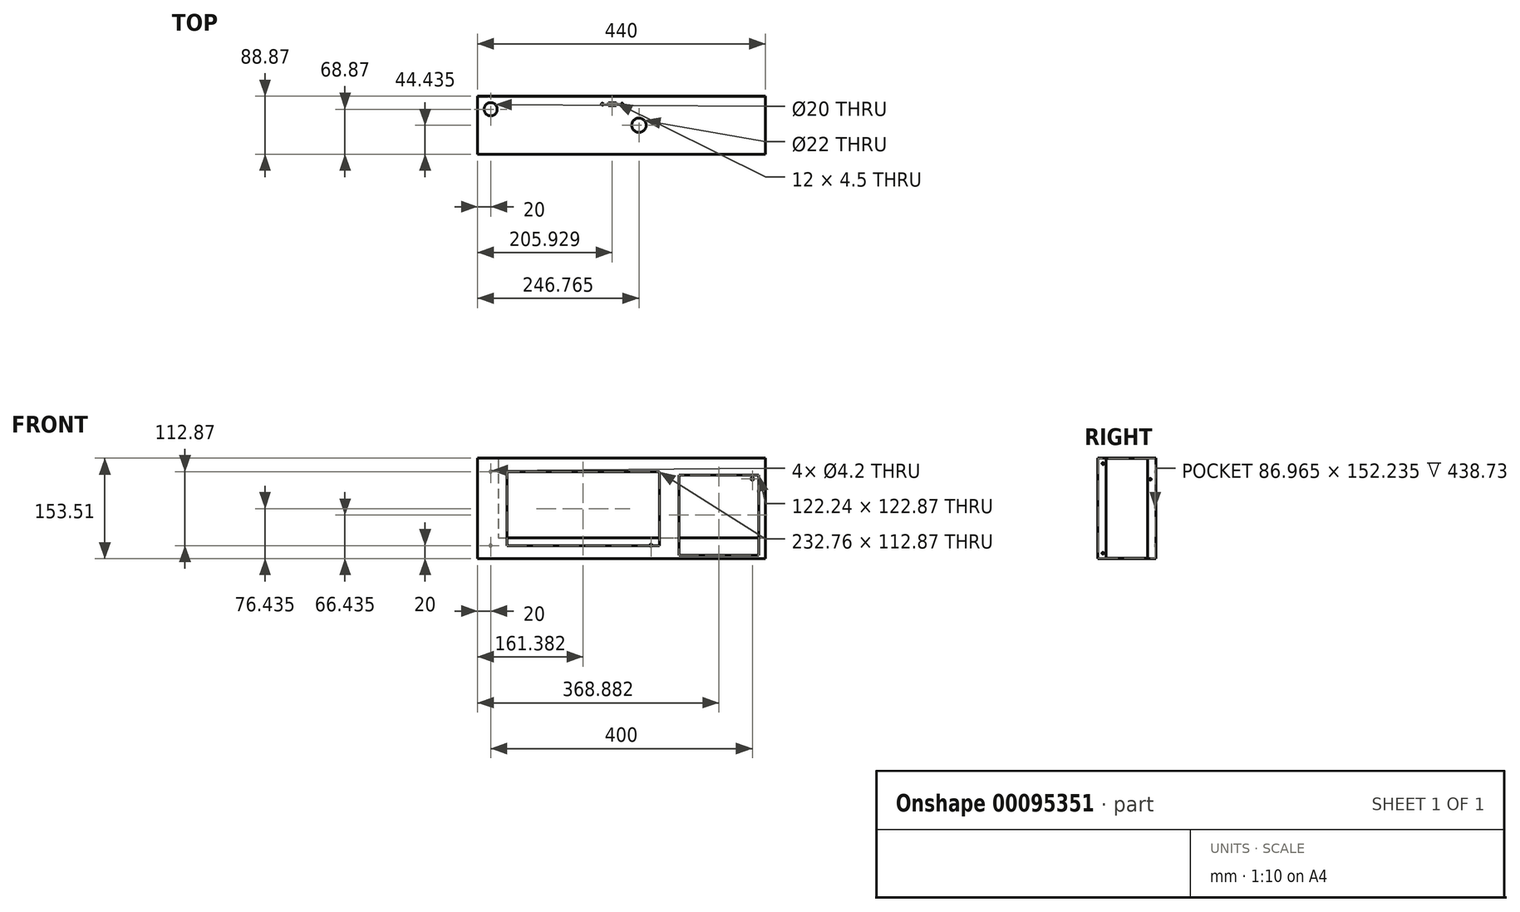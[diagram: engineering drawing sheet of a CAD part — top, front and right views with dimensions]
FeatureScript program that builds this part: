
annotation { "Feature Type Name" : "Feature", "Feature Type Description" : "" }
export const myFeature = defineFeature(function(context is Context, id is Id, definition is map)
    precondition{}
    {
        {
            var Q0;
            Q0=qCreatedBy(makeId("Top.planeOp"),FACE);
            var sketch = newSketch(context, id + "F0", { "sketchPlane" : qUnion([Q0])});
            skLineSegment(sketch, "E0.bottom", {"start": v(0, 0) * mm, "end": v(440, 0) * mm});
            skLineSegment(sketch, "E0.top", {"start": v(0, -88.87) * mm, "end": v(440, -88.87) * mm});
            skLineSegment(sketch, "E0.left", {"start": v(0, 0) * mm, "end": v(0, -88.87) * mm});
            skLineSegment(sketch, "E0.right", {"start": v(440, 0) * mm, "end": v(440, -88.87) * mm});
            skLineSegment(sketch, "E1", {"start": v(297.76, 0) * mm, "end": v(297.76, -88.87) * mm, "construction": true});
            skCircle(sketch, "E2", {"center": v(20, -20) * mm, "radius": 10 * mm});
            skCircle(sketch, "E3", {"center": v(246.76, -44.43) * mm, "radius": 11 * mm});
            skLineSegment(sketch, "E4.bottom", {"start": v(211.93, -14.5) * mm, "end": v(199.93, -14.5) * mm});
            skLineSegment(sketch, "E4.top", {"start": v(211.93, -10) * mm, "end": v(199.93, -10) * mm});
            skLineSegment(sketch, "E4.left", {"start": v(211.93, -14.5) * mm, "end": v(211.93, -10) * mm});
            skLineSegment(sketch, "E4.right", {"start": v(199.93, -14.5) * mm, "end": v(199.93, -10) * mm});
            skPoint(sketch, "E4.middle", {"position": v(205.93, -12.25) * mm});
            skPoint(sketch, "E5", {"position": v(297.76, -44.43) * mm});
            skCircle(sketch, "E6", {"center": v(220.93, -12.25) * mm, "radius": 1.6 * mm});
            skCircle(sketch, "E7", {"center": v(190.93, -12.25) * mm, "radius": 1.6 * mm});
            skLineSegment(sketch, "E8", {"start": v(205.93, -10) * mm, "end": v(205.93, -14.5) * mm, "construction": true});
            skSolve(sketch);
        }
        {
            var Q0;
            Q0=makeQuery(id+"F0.imprint","IMPRINT",FACE,{"disambiguationData":[TD([[makeQuery(id+"F0.imprint","IMPRINT",EDGE,{"derivedFrom":sQuery(id+"F0.wireOp",EDGE,"E0.bottom")}),-1.0]])]});
            extrude(context, id + "F1", {"entities" : qUnion([Q0]), "depth" : .635 * mm});
        }
        {
            var Q0;
            Q0=qCreatedBy(makeId("Front.planeOp"),FACE);
            var sketch = newSketch(context, id + "F2", { "sketchPlane" : qUnion([Q0])});
            skLineSegment(sketch, "E9.0", {"start": v(0, 0) * mm, "end": v(440, 0) * mm});
            skLineSegment(sketch, "E10.top", {"start": v(0, -152.87) * mm, "end": v(440, -152.87) * mm});
            skLineSegment(sketch, "E10.left", {"start": v(0, 0) * mm, "end": v(0, -152.87) * mm});
            skLineSegment(sketch, "E10.right", {"start": v(440, 0) * mm, "end": v(440, -152.87) * mm});
            skCircle(sketch, "E11", {"center": v(20, -20) * mm, "radius": 2.1 * mm});
            skCircle(sketch, "E12", {"center": v(20, -132.87) * mm, "radius": 2.1 * mm});
            skCircle(sketch, "E13", {"center": v(265.14, -132.87) * mm, "radius": 2.1 * mm});
            skPoint(sketch, "E14.0", {"position": v(297.76, 0) * mm});
            skLineSegment(sketch, "E15", {"start": v(297.76, 0) * mm, "end": v(297.76, -152.87) * mm, "construction": true});
            skCircle(sketch, "E16", {"center": v(420, -30.93) * mm, "radius": 2.1 * mm});
            skSolve(sketch);
        }
        {
            var Q0;
            Q0=makeQuery(id+"F2.imprint","IMPRINT",FACE,{"disambiguationData":[TD([[makeQuery(id+"F2.imprint","IMPRINT",EDGE,{"derivedFrom":sQuery(id+"F2.wireOp",EDGE,"E9.0")}),-1.0]])]});
            extrude(context, id + "F3", {"entities" : qUnion([Q0]), "operationType" : NewBodyOperationType.ADD, "depth" : .635 * mm});
        }
        {
            var Q0;
            Q0=makeQuery(id+"F1.opExtrude","SWEPT_FACE",FACE,{"disambiguationData":[OSD([sQuery(id+"F0.wireOp",EDGE,"E0.top")])]});
            var sketch = newSketch(context, id + "F4", { "sketchPlane" : qUnion([Q0])});
            skLineSegment(sketch, "E17.0", {"start": v(0, 0) * mm, "end": v(440, 0) * mm});
            skLineSegment(sketch, "E18.0", {"start": v(0, -152.87) * mm, "end": v(440, -152.87) * mm});
            skLineSegment(sketch, "E19", {"start": v(0, 0.63) * mm, "end": v(0, -152.87) * mm});
            skLineSegment(sketch, "E20", {"start": v(440, 0.63) * mm, "end": v(440, -152.87) * mm});
            skPoint(sketch, "E21.0", {"position": v(297.76, 0) * mm});
            skLineSegment(sketch, "E22", {"start": v(297.76, 0) * mm, "end": v(297.76, -152.87) * mm, "construction": true});
            skLineSegment(sketch, "E23.bottom", {"start": v(45, -20) * mm, "end": v(277.76, -20) * mm});
            skLineSegment(sketch, "E23.top", {"start": v(45, -132.87) * mm, "end": v(277.76, -132.87) * mm});
            skLineSegment(sketch, "E23.left", {"start": v(45, -20) * mm, "end": v(45, -132.87) * mm});
            skLineSegment(sketch, "E23.right", {"start": v(277.76, -20) * mm, "end": v(277.76, -132.87) * mm});
            skLineSegment(sketch, "E24.bottom", {"start": v(307.76, -25) * mm, "end": v(430, -25) * mm});
            skLineSegment(sketch, "E24.top", {"start": v(307.76, -147.87) * mm, "end": v(430, -147.87) * mm});
            skLineSegment(sketch, "E24.left", {"start": v(307.76, -25) * mm, "end": v(307.76, -147.87) * mm});
            skLineSegment(sketch, "E24.right", {"start": v(430, -25) * mm, "end": v(430, -147.87) * mm});
            skSolve(sketch);
        }
        {
            var Q0;
            {var subQ2=sQuery(id+"F4.wireOp",EDGE,"E17.0");Q0=makeQuery(id+"F4.imprint","IMPRINT",FACE,{"disambiguationData":[TD([[makeQuery(id+"F4.imprint","IMPRINT",EDGE,{"derivedFrom":subQ2}),-1.0]])]});}
            extrude(context, id + "F5", {"entities" : qUnion([Q0]), "operationType" : NewBodyOperationType.ADD, "oppositeDirection" : true, "depth" : .635 * mm});
        }
        {
            var Q0;
            Q0=makeQuery(id+"F5.opExtrude","SWEPT_FACE",FACE,{"disambiguationData":[OSD([sQuery(id+"F4.wireOp",EDGE,"E18.0")])]});
            var sketch = newSketch(context, id + "F6", { "sketchPlane" : qUnion([Q0])});
            skLineSegment(sketch, "E25.0", {"start": v(0, 0.64) * mm, "end": v(440, 0.64) * mm});
            skLineSegment(sketch, "E26.0", {"start": v(0, 88.87) * mm, "end": v(440, 88.87) * mm});
            skLineSegment(sketch, "E27", {"start": v(0, 0.63) * mm, "end": v(0, 88.87) * mm});
            skLineSegment(sketch, "E28", {"start": v(440, 88.87) * mm, "end": v(440, 0.63) * mm});
            skSolve(sketch);
        }
        {
            var Q0;
            {var subQ0=sQuery(id+"F6.wireOp",EDGE,"E25.0");Q0=makeQuery(id+"F6.imprint","IMPRINT",FACE,{"disambiguationData":[TD([[makeQuery(id+"F6.imprint","IMPRINT",EDGE,{"derivedFrom":subQ0}),1.0]])]});}
            extrude(context, id + "F7", {"entities" : qUnion([Q0]), "operationType" : NewBodyOperationType.ADD, "oppositeDirection" : true, "depth" : .635 * mm});
        }
        {
            var Q0;
            Q0=makeQuery(id+"F3.opExtrude","CAP_FACE",FACE,{"disambiguationData":[OSD([sQuery(id+"F2.wireOp",EDGE,"E9.0"),sQuery(id+"F2.wireOp",EDGE,"E10.top"),sQuery(id+"F2.wireOp",EDGE,"E10.left"),sQuery(id+"F2.wireOp",EDGE,"E10.right"),sQuery(id+"F2.wireOp",EDGE,"E11"),sQuery(id+"F2.wireOp",EDGE,"E12"),sQuery(id+"F2.wireOp",EDGE,"E13"),sQuery(id+"F2.wireOp",EDGE,"E16")])],"isStart":false});
            var sketch = newSketch(context, id + "F8", { "sketchPlane" : qUnion([Q0])});
            skLineSegment(sketch, "E29.0", {"start": v(0, -152.24) * mm, "end": v(440, -152.24) * mm});
            skCircle(sketch, "E30.0", {"center": v(20, -132.87) * mm, "radius": 2.1 * mm});
            skCircle(sketch, "E30.1", {"center": v(265.14, -132.87) * mm, "radius": 2.1 * mm});
            skLineSegment(sketch, "E30.2", {"start": v(297.76, 0) * mm, "end": v(297.76, -152.87) * mm, "construction": true});
            skLineSegment(sketch, "E31", {"start": v(0, -121.27) * mm, "end": v(440, -121.27) * mm});
            skSolve(sketch);
        }
        {
            var Q0;
            {var subQ1=sQuery(id+"F8.wireOp",EDGE,"E29.0");Q0=makeQuery(id+"F8.imprint","IMPRINT",FACE,{"disambiguationData":[TD([[makeQuery(id+"F8.imprint","IMPRINT",EDGE,{"derivedFrom":subQ1}),1.0]])]});}
            extrude(context, id + "F9", {"entities" : qUnion([Q0]), "operationType" : NewBodyOperationType.ADD, "depth" : .635 * mm});
        }
        {
            var Q0;
            {var subQ0=sQuery(id+"F2.wireOp",EDGE,"E10.left");Q0=makeQuery(id+"F9.boolean.opBoolean","MERGE",FACE,{"derivedFrom":[makeQuery(id+"F7.boolean.opBoolean","MERGE",FACE,{"derivedFrom":[makeQuery(id+"F5.boolean.opBoolean","MERGE",FACE,{"derivedFrom":[makeQuery(id+"F3.boolean.opBoolean","MERGE",FACE,{"derivedFrom":[makeQuery(id+"F1.opExtrude","SWEPT_FACE",FACE,{"disambiguationData":[OSD([sQuery(id+"F0.wireOp",EDGE,"E0.left")])]}),makeQuery(id+"F3.opExtrude","SWEPT_FACE",FACE,{"disambiguationData":[OSD([subQ0])]})]}),makeQuery(id+"F5.opExtrude","SWEPT_FACE",FACE,{"disambiguationData":[OSD([sQuery(id+"F4.wireOp",EDGE,"E19")])]})]}),makeQuery(id+"F7.opExtrude","SWEPT_FACE",FACE,{"disambiguationData":[OSD([sQuery(id+"F6.wireOp",EDGE,"E27")])]})]}),makeQuery(id+"F9.opExtrude","SWEPT_FACE",FACE,{"disambiguationData":[OSD([subQ0])]})]});}
            var sketch = newSketch(context, id + "F10", { "sketchPlane" : qUnion([Q0])});
            skLineSegment(sketch, "E32.0", {"start": v(0.64, 0) * mm, "end": v(88.24, 0) * mm});
            skLineSegment(sketch, "E32.1", {"start": v(88.24, 0) * mm, "end": v(88.24, -152.24) * mm});
            skLineSegment(sketch, "E32.2", {"start": v(1.27, -152.24) * mm, "end": v(88.24, -152.24) * mm});
            skSolve(sketch);
        }
        {
            var Q0;
            Q0=makeQuery(id+"F3.opExtrude","CAP_FACE",FACE,{"disambiguationData":[OSD([sQuery(id+"F2.wireOp",EDGE,"E9.0"),sQuery(id+"F2.wireOp",EDGE,"E10.top"),sQuery(id+"F2.wireOp",EDGE,"E10.left"),sQuery(id+"F2.wireOp",EDGE,"E10.right"),sQuery(id+"F2.wireOp",EDGE,"E11"),sQuery(id+"F2.wireOp",EDGE,"E12"),sQuery(id+"F2.wireOp",EDGE,"E13"),sQuery(id+"F2.wireOp",EDGE,"E16")])],"isStart":false});
            var sketch = newSketch(context, id + "F11", { "sketchPlane" : qUnion([Q0])});
            skCircle(sketch, "E33.0", {"center": v(20, -20) * mm, "radius": 2.1 * mm});
            skCircle(sketch, "E33.1", {"center": v(20, -132.87) * mm, "radius": 2.1 * mm});
            skLineSegment(sketch, "E33.2", {"start": v(0, 0) * mm, "end": v(0, -121.27) * mm});
            skLineSegment(sketch, "E33.3", {"start": v(0, -121.27) * mm, "end": v(0, -152.24) * mm});
            skLineSegment(sketch, "E34", {"start": v(31.6, 0) * mm, "end": v(31.6, -152.24) * mm});
            skLineSegment(sketch, "E35", {"start": v(31.6, -152.24) * mm, "end": v(0, -152.24) * mm});
            skSolve(sketch);
        }
        {
            var Q0;
            Q0=makeQuery(id+"F11.imprint","IMPRINT",FACE,{"disambiguationData":[TD([[makeQuery(id+"F11.imprint","IMPRINT",EDGE,{"derivedFrom":sQuery(id+"F11.wireOp",EDGE,"E33.0")}),-1.0]])]});
            extrude(context, id + "F12", {"entities" : qUnion([Q0]), "operationType" : NewBodyOperationType.ADD, "depth" : .635 * mm});
        }
        {
            var Q0;
            Q0=makeQuery(id+"F10.imprint","IMPRINT",FACE,{"disambiguationData":[TD([[makeQuery(id+"F10.imprint","IMPRINT",EDGE,{"derivedFrom":sQuery(id+"F10.wireOp",EDGE,"E32.0")}),-1.0]])]});
            extrude(context, id + "F13", {"entities" : qUnion([Q0]), "operationType" : NewBodyOperationType.ADD, "oppositeDirection" : true, "depth" : .635 * mm});
        }
        {
            var Q0;
            {var subQ0=sQuery(id+"F2.wireOp",EDGE,"E10.right");Q0=makeQuery(id+"F9.boolean.opBoolean","MERGE",FACE,{"derivedFrom":[makeQuery(id+"F7.boolean.opBoolean","MERGE",FACE,{"derivedFrom":[makeQuery(id+"F5.boolean.opBoolean","MERGE",FACE,{"derivedFrom":[makeQuery(id+"F3.boolean.opBoolean","MERGE",FACE,{"derivedFrom":[makeQuery(id+"F1.opExtrude","SWEPT_FACE",FACE,{"disambiguationData":[OSD([sQuery(id+"F0.wireOp",EDGE,"E0.right")])]}),makeQuery(id+"F3.opExtrude","SWEPT_FACE",FACE,{"disambiguationData":[OSD([subQ0])]})]}),makeQuery(id+"F5.opExtrude","SWEPT_FACE",FACE,{"disambiguationData":[OSD([sQuery(id+"F4.wireOp",EDGE,"E20")])]})]}),makeQuery(id+"F7.opExtrude","SWEPT_FACE",FACE,{"disambiguationData":[OSD([sQuery(id+"F6.wireOp",EDGE,"E28")])]})]}),makeQuery(id+"F9.opExtrude","SWEPT_FACE",FACE,{"disambiguationData":[OSD([subQ0])]})]});}
            var sketch = newSketch(context, id + "F14", { "sketchPlane" : qUnion([Q0])});
            skLineSegment(sketch, "E36.0", {"start": v(-88.24, 0) * mm, "end": v(-88.24, -152.24) * mm});
            skLineSegment(sketch, "E36.1", {"start": v(-0.64, 0) * mm, "end": v(-88.24, 0) * mm});
            skLineSegment(sketch, "E36.2", {"start": v(-0.64, 0) * mm, "end": v(-0.64, -121.27) * mm});
            skLineSegment(sketch, "E36.3", {"start": v(-88.24, -152.24) * mm, "end": v(-1.27, -152.24) * mm});
            skLineSegment(sketch, "E37", {"start": v(-0.64, -121.27) * mm, "end": v(-0.64, -152.24) * mm});
            skLineSegment(sketch, "E38", {"start": v(-0.64, -152.24) * mm, "end": v(-1.27, -152.24) * mm});
            skLineSegment(sketch, "E39", {"start": v(-76.14, 0) * mm, "end": v(-76.14, -152.24) * mm});
            skLineSegment(sketch, "E40", {"start": v(-12.74, 0) * mm, "end": v(-12.74, -152.24) * mm});
            skCircle(sketch, "E41", {"center": v(-8.24, -31.6) * mm, "radius": 1.5 * mm});
            skCircle(sketch, "E42", {"center": v(-80.64, -144.64) * mm, "radius": 1.5 * mm});
            skCircle(sketch, "E43", {"center": v(-80.64, -7.6) * mm, "radius": 1.5 * mm});
            skCircle(sketch, "E44", {"center": v(-18.24, -144.64) * mm, "radius": 1.5 * mm});
            skSolve(sketch);
        }
        {
            var Q0;
            {var subQ1=sQuery(id+"F14.wireOp",EDGE,"E36.0");Q0=makeQuery(id+"F14.imprint","IMPRINT",FACE,{"disambiguationData":[TD([[makeQuery(id+"F14.imprint","IMPRINT",EDGE,{"derivedFrom":subQ1}),1.0]])]});}
            var Q1;
            {var subQ4=sQuery(id+"F14.wireOp",EDGE,"E36.2");Q1=makeQuery(id+"F14.imprint","IMPRINT",FACE,{"disambiguationData":[TD([[makeQuery(id+"F14.imprint","IMPRINT",EDGE,{"derivedFrom":subQ4}),-1.0]])]});}
            extrude(context, id + "F15", {"entities" : qUnion([Q0, Q1]), "operationType" : NewBodyOperationType.ADD, "oppositeDirection" : true, "depth" : .635 * mm});
        }
    });
